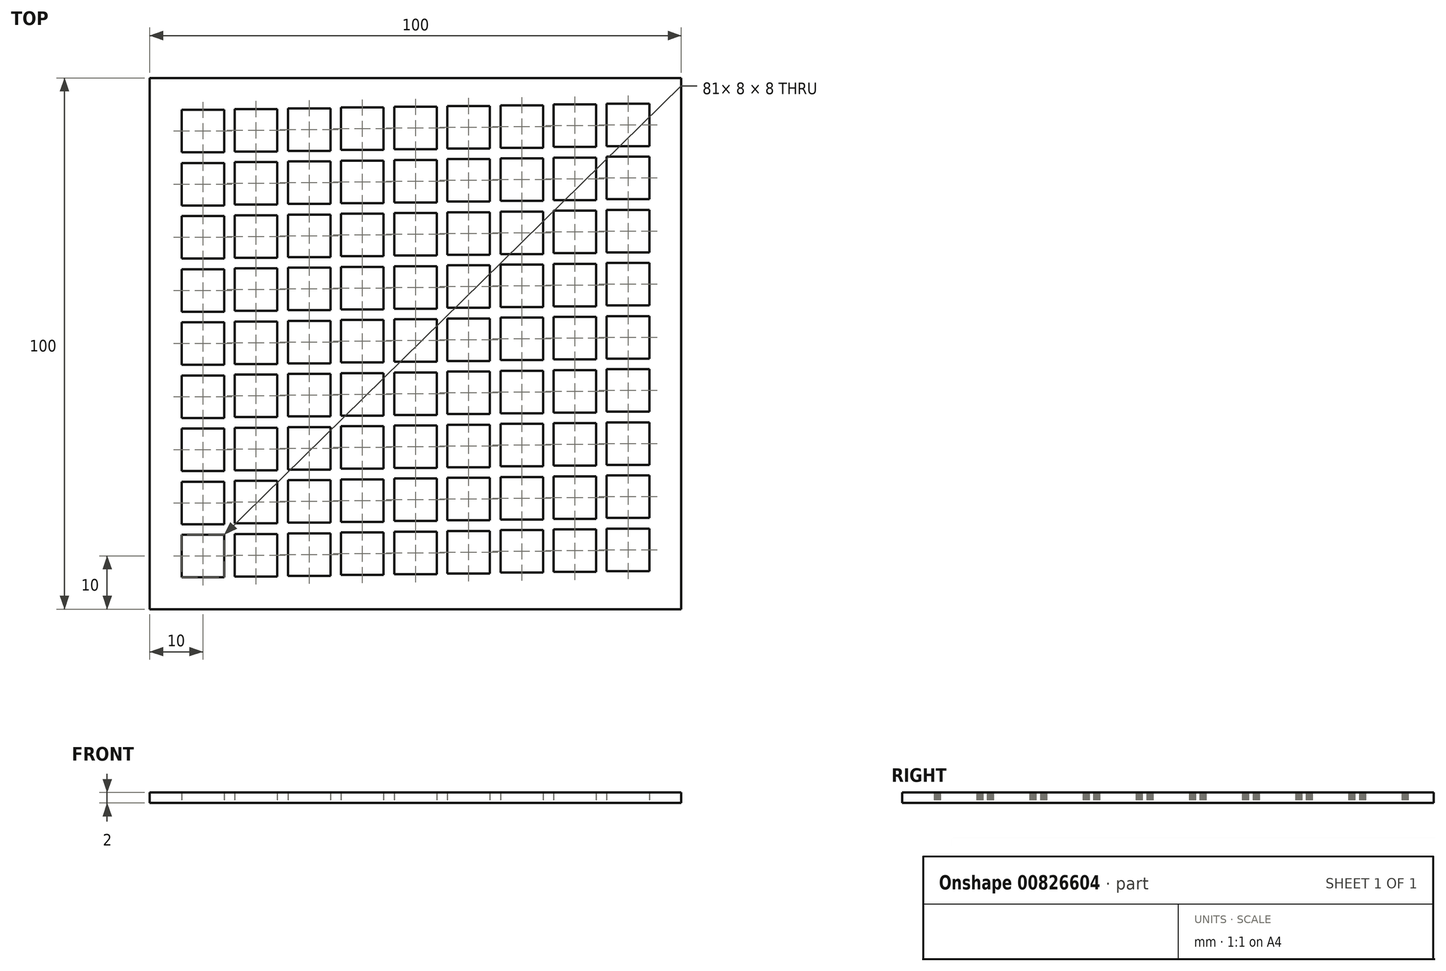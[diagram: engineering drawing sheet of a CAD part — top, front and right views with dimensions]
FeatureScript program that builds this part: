
annotation { "Feature Type Name" : "Feature", "Feature Type Description" : "" }
export const myFeature = defineFeature(function(context is Context, id is Id, definition is map)
    precondition{}
    {
        {
            var Q0;
            Q0=qCreatedBy(makeId("Top.planeOp"),FACE);
            var sketch = newSketch(context, id + "F0", { "sketchPlane" : qUnion([Q0])});
            skLineSegment(sketch, "E0.bottom", {"start": v(-50, 50) * mm, "end": v(50, 50) * mm});
            skLineSegment(sketch, "E0.top", {"start": v(-50, -50) * mm, "end": v(50, -50) * mm});
            skLineSegment(sketch, "E0.left", {"start": v(-50, 50) * mm, "end": v(-50, -50) * mm});
            skLineSegment(sketch, "E0.right", {"start": v(50, 50) * mm, "end": v(50, -50) * mm});
            skLineSegment(sketch, "E1", {"start": v(-50, 50) * mm, "end": v(50, -50) * mm, "construction": true});
            skLineSegment(sketch, "E2", {"start": v(50, 50) * mm, "end": v(-50, -50) * mm, "construction": true});
            skPoint(sketch, "E3", {"position": v(0, 0) * mm});
            skSolve(sketch);
        }
        {
            var Q0;
            Q0 = qSketchRegion(id + "F0", true);
            extrude(context, id + "F1", {"entities" : qUnion([Q0]), "depth" : 2 * mm, "offsetDistance" : 25 * mm});
        }
        {
            var Q0;
            Q0=qCreatedBy(makeId("Top.planeOp"),FACE);
            var sketch = newSketch(context, id + "F2", { "sketchPlane" : qUnion([Q0])});
            skLineSegment(sketch, "E4.bottom", {"start": v(-44, 44) * mm, "end": v(-36, 44) * mm});
            skLineSegment(sketch, "E4.top", {"start": v(-44, 36) * mm, "end": v(-36, 36) * mm});
            skLineSegment(sketch, "E4.left", {"start": v(-44, 44) * mm, "end": v(-44, 36) * mm});
            skLineSegment(sketch, "E4.right", {"start": v(-36, 44) * mm, "end": v(-36, 36) * mm});
            skLineSegment(sketch, "E5.0.1.0", {"start": v(-44, 34) * mm, "end": v(-36, 34) * mm});
            skLineSegment(sketch, "E5.0.1.1", {"start": v(-44, 26) * mm, "end": v(-36, 26) * mm});
            skLineSegment(sketch, "E5.0.1.2", {"start": v(-44, 34) * mm, "end": v(-44, 26) * mm});
            skLineSegment(sketch, "E5.0.1.3", {"start": v(-36, 34) * mm, "end": v(-36, 26) * mm});
            skLineSegment(sketch, "E5.0.2.0", {"start": v(-44, 24) * mm, "end": v(-36, 24) * mm});
            skLineSegment(sketch, "E5.0.2.1", {"start": v(-44, 16) * mm, "end": v(-36, 16) * mm});
            skLineSegment(sketch, "E5.0.2.2", {"start": v(-44, 24) * mm, "end": v(-44, 16) * mm});
            skLineSegment(sketch, "E5.0.2.3", {"start": v(-36, 24) * mm, "end": v(-36, 16) * mm});
            skLineSegment(sketch, "E5.0.3.0", {"start": v(-44, 14) * mm, "end": v(-36, 14) * mm});
            skLineSegment(sketch, "E5.0.3.1", {"start": v(-44, 6) * mm, "end": v(-36, 6) * mm});
            skLineSegment(sketch, "E5.0.3.2", {"start": v(-44, 14) * mm, "end": v(-44, 6) * mm});
            skLineSegment(sketch, "E5.0.3.3", {"start": v(-36, 14) * mm, "end": v(-36, 6) * mm});
            skLineSegment(sketch, "E5.0.4.0", {"start": v(-44, 4) * mm, "end": v(-36, 4) * mm});
            skLineSegment(sketch, "E5.0.4.1", {"start": v(-44, -4) * mm, "end": v(-36, -4) * mm});
            skLineSegment(sketch, "E5.0.4.2", {"start": v(-44, 4) * mm, "end": v(-44, -4) * mm});
            skLineSegment(sketch, "E5.0.4.3", {"start": v(-36, 4) * mm, "end": v(-36, -4) * mm});
            skLineSegment(sketch, "E5.0.5.0", {"start": v(-44, -6) * mm, "end": v(-36, -6) * mm});
            skLineSegment(sketch, "E5.0.5.1", {"start": v(-44, -14) * mm, "end": v(-36, -14) * mm});
            skLineSegment(sketch, "E5.0.5.2", {"start": v(-44, -6) * mm, "end": v(-44, -14) * mm});
            skLineSegment(sketch, "E5.0.5.3", {"start": v(-36, -6) * mm, "end": v(-36, -14) * mm});
            skLineSegment(sketch, "E5.0.6.0", {"start": v(-44, -16) * mm, "end": v(-36, -16) * mm});
            skLineSegment(sketch, "E5.0.6.1", {"start": v(-44, -24) * mm, "end": v(-36, -24) * mm});
            skLineSegment(sketch, "E5.0.6.2", {"start": v(-44, -16) * mm, "end": v(-44, -24) * mm});
            skLineSegment(sketch, "E5.0.6.3", {"start": v(-36, -16) * mm, "end": v(-36, -24) * mm});
            skLineSegment(sketch, "E5.0.7.0", {"start": v(-44, -26) * mm, "end": v(-36, -26) * mm});
            skLineSegment(sketch, "E5.0.7.1", {"start": v(-44, -34) * mm, "end": v(-36, -34) * mm});
            skLineSegment(sketch, "E5.0.7.2", {"start": v(-44, -26) * mm, "end": v(-44, -34) * mm});
            skLineSegment(sketch, "E5.0.7.3", {"start": v(-36, -26) * mm, "end": v(-36, -34) * mm});
            skLineSegment(sketch, "E5.0.8.0", {"start": v(-44, -36) * mm, "end": v(-36, -36) * mm});
            skLineSegment(sketch, "E5.0.8.1", {"start": v(-44, -44) * mm, "end": v(-36, -44) * mm});
            skLineSegment(sketch, "E5.0.8.2", {"start": v(-44, -36) * mm, "end": v(-44, -44) * mm});
            skLineSegment(sketch, "E5.0.8.3", {"start": v(-36, -36) * mm, "end": v(-36, -44) * mm});
            skLineSegment(sketch, "E5.1.0.0", {"start": v(-34, 44.14) * mm, "end": v(-26, 44.14) * mm});
            skLineSegment(sketch, "E5.1.0.1", {"start": v(-34, 36.14) * mm, "end": v(-26, 36.14) * mm});
            skLineSegment(sketch, "E5.1.0.2", {"start": v(-34, 44.14) * mm, "end": v(-34, 36.14) * mm});
            skLineSegment(sketch, "E5.1.0.3", {"start": v(-26, 44.14) * mm, "end": v(-26, 36.14) * mm});
            skLineSegment(sketch, "E5.1.1.0", {"start": v(-34, 34.14) * mm, "end": v(-26, 34.14) * mm});
            skLineSegment(sketch, "E5.1.1.1", {"start": v(-34, 26.14) * mm, "end": v(-26, 26.14) * mm});
            skLineSegment(sketch, "E5.1.1.2", {"start": v(-34, 34.14) * mm, "end": v(-34, 26.14) * mm});
            skLineSegment(sketch, "E5.1.1.3", {"start": v(-26, 34.14) * mm, "end": v(-26, 26.14) * mm});
            skLineSegment(sketch, "E5.1.2.0", {"start": v(-34, 24.14) * mm, "end": v(-26, 24.14) * mm});
            skLineSegment(sketch, "E5.1.2.1", {"start": v(-34, 16.14) * mm, "end": v(-26, 16.14) * mm});
            skLineSegment(sketch, "E5.1.2.2", {"start": v(-34, 24.14) * mm, "end": v(-34, 16.14) * mm});
            skLineSegment(sketch, "E5.1.2.3", {"start": v(-26, 24.14) * mm, "end": v(-26, 16.14) * mm});
            skLineSegment(sketch, "E5.1.3.0", {"start": v(-34, 14.14) * mm, "end": v(-26, 14.14) * mm});
            skLineSegment(sketch, "E5.1.3.1", {"start": v(-34, 6.14) * mm, "end": v(-26, 6.14) * mm});
            skLineSegment(sketch, "E5.1.3.2", {"start": v(-34, 14.14) * mm, "end": v(-34, 6.14) * mm});
            skLineSegment(sketch, "E5.1.3.3", {"start": v(-26, 14.14) * mm, "end": v(-26, 6.14) * mm});
            skLineSegment(sketch, "E5.1.4.0", {"start": v(-34, 4.14) * mm, "end": v(-26, 4.14) * mm});
            skLineSegment(sketch, "E5.1.4.1", {"start": v(-34, -3.86) * mm, "end": v(-26, -3.86) * mm});
            skLineSegment(sketch, "E5.1.4.2", {"start": v(-34, 4.14) * mm, "end": v(-34, -3.86) * mm});
            skLineSegment(sketch, "E5.1.4.3", {"start": v(-26, 4.14) * mm, "end": v(-26, -3.86) * mm});
            skLineSegment(sketch, "E5.1.5.0", {"start": v(-34, -5.86) * mm, "end": v(-26, -5.86) * mm});
            skLineSegment(sketch, "E5.1.5.1", {"start": v(-34, -13.86) * mm, "end": v(-26, -13.86) * mm});
            skLineSegment(sketch, "E5.1.5.2", {"start": v(-34, -5.86) * mm, "end": v(-34, -13.86) * mm});
            skLineSegment(sketch, "E5.1.5.3", {"start": v(-26, -5.86) * mm, "end": v(-26, -13.86) * mm});
            skLineSegment(sketch, "E5.1.6.0", {"start": v(-34, -15.86) * mm, "end": v(-26, -15.86) * mm});
            skLineSegment(sketch, "E5.1.6.1", {"start": v(-34, -23.86) * mm, "end": v(-26, -23.86) * mm});
            skLineSegment(sketch, "E5.1.6.2", {"start": v(-34, -15.86) * mm, "end": v(-34, -23.86) * mm});
            skLineSegment(sketch, "E5.1.6.3", {"start": v(-26, -15.86) * mm, "end": v(-26, -23.86) * mm});
            skLineSegment(sketch, "E5.1.7.0", {"start": v(-34, -25.86) * mm, "end": v(-26, -25.86) * mm});
            skLineSegment(sketch, "E5.1.7.1", {"start": v(-34, -33.86) * mm, "end": v(-26, -33.86) * mm});
            skLineSegment(sketch, "E5.1.7.2", {"start": v(-34, -25.86) * mm, "end": v(-34, -33.86) * mm});
            skLineSegment(sketch, "E5.1.7.3", {"start": v(-26, -25.86) * mm, "end": v(-26, -33.86) * mm});
            skLineSegment(sketch, "E5.1.8.0", {"start": v(-34, -35.86) * mm, "end": v(-26, -35.86) * mm});
            skLineSegment(sketch, "E5.1.8.1", {"start": v(-34, -43.86) * mm, "end": v(-26, -43.86) * mm});
            skLineSegment(sketch, "E5.1.8.2", {"start": v(-34, -35.86) * mm, "end": v(-34, -43.86) * mm});
            skLineSegment(sketch, "E5.1.8.3", {"start": v(-26, -35.86) * mm, "end": v(-26, -43.86) * mm});
            skLineSegment(sketch, "E5.2.0.0", {"start": v(-24, 44.29) * mm, "end": v(-16, 44.29) * mm});
            skLineSegment(sketch, "E5.2.0.1", {"start": v(-24, 36.29) * mm, "end": v(-16, 36.29) * mm});
            skLineSegment(sketch, "E5.2.0.2", {"start": v(-24, 44.29) * mm, "end": v(-24, 36.29) * mm});
            skLineSegment(sketch, "E5.2.0.3", {"start": v(-16, 44.29) * mm, "end": v(-16, 36.29) * mm});
            skLineSegment(sketch, "E5.2.1.0", {"start": v(-24, 34.29) * mm, "end": v(-16, 34.29) * mm});
            skLineSegment(sketch, "E5.2.1.1", {"start": v(-24, 26.29) * mm, "end": v(-16, 26.29) * mm});
            skLineSegment(sketch, "E5.2.1.2", {"start": v(-24, 34.29) * mm, "end": v(-24, 26.29) * mm});
            skLineSegment(sketch, "E5.2.1.3", {"start": v(-16, 34.29) * mm, "end": v(-16, 26.29) * mm});
            skLineSegment(sketch, "E5.2.2.0", {"start": v(-24, 24.29) * mm, "end": v(-16, 24.29) * mm});
            skLineSegment(sketch, "E5.2.2.1", {"start": v(-24, 16.29) * mm, "end": v(-16, 16.29) * mm});
            skLineSegment(sketch, "E5.2.2.2", {"start": v(-24, 24.29) * mm, "end": v(-24, 16.29) * mm});
            skLineSegment(sketch, "E5.2.2.3", {"start": v(-16, 24.29) * mm, "end": v(-16, 16.29) * mm});
            skLineSegment(sketch, "E5.2.3.0", {"start": v(-24, 14.29) * mm, "end": v(-16, 14.29) * mm});
            skLineSegment(sketch, "E5.2.3.1", {"start": v(-24, 6.29) * mm, "end": v(-16, 6.29) * mm});
            skLineSegment(sketch, "E5.2.3.2", {"start": v(-24, 14.29) * mm, "end": v(-24, 6.29) * mm});
            skLineSegment(sketch, "E5.2.3.3", {"start": v(-16, 14.29) * mm, "end": v(-16, 6.29) * mm});
            skLineSegment(sketch, "E5.2.4.0", {"start": v(-24, 4.29) * mm, "end": v(-16, 4.29) * mm});
            skLineSegment(sketch, "E5.2.4.1", {"start": v(-24, -3.71) * mm, "end": v(-16, -3.71) * mm});
            skLineSegment(sketch, "E5.2.4.2", {"start": v(-24, 4.29) * mm, "end": v(-24, -3.71) * mm});
            skLineSegment(sketch, "E5.2.4.3", {"start": v(-16, 4.29) * mm, "end": v(-16, -3.71) * mm});
            skLineSegment(sketch, "E5.2.5.0", {"start": v(-24, -5.71) * mm, "end": v(-16, -5.71) * mm});
            skLineSegment(sketch, "E5.2.5.1", {"start": v(-24, -13.71) * mm, "end": v(-16, -13.71) * mm});
            skLineSegment(sketch, "E5.2.5.2", {"start": v(-24, -5.71) * mm, "end": v(-24, -13.71) * mm});
            skLineSegment(sketch, "E5.2.5.3", {"start": v(-16, -5.71) * mm, "end": v(-16, -13.71) * mm});
            skLineSegment(sketch, "E5.2.6.0", {"start": v(-24, -15.71) * mm, "end": v(-16, -15.71) * mm});
            skLineSegment(sketch, "E5.2.6.1", {"start": v(-24, -23.71) * mm, "end": v(-16, -23.71) * mm});
            skLineSegment(sketch, "E5.2.6.2", {"start": v(-24, -15.71) * mm, "end": v(-24, -23.71) * mm});
            skLineSegment(sketch, "E5.2.6.3", {"start": v(-16, -15.71) * mm, "end": v(-16, -23.71) * mm});
            skLineSegment(sketch, "E5.2.7.0", {"start": v(-24, -25.71) * mm, "end": v(-16, -25.71) * mm});
            skLineSegment(sketch, "E5.2.7.1", {"start": v(-24, -33.71) * mm, "end": v(-16, -33.71) * mm});
            skLineSegment(sketch, "E5.2.7.2", {"start": v(-24, -25.71) * mm, "end": v(-24, -33.71) * mm});
            skLineSegment(sketch, "E5.2.7.3", {"start": v(-16, -25.71) * mm, "end": v(-16, -33.71) * mm});
            skLineSegment(sketch, "E5.2.8.0", {"start": v(-24, -35.71) * mm, "end": v(-16, -35.71) * mm});
            skLineSegment(sketch, "E5.2.8.1", {"start": v(-24, -43.71) * mm, "end": v(-16, -43.71) * mm});
            skLineSegment(sketch, "E5.2.8.2", {"start": v(-24, -35.71) * mm, "end": v(-24, -43.71) * mm});
            skLineSegment(sketch, "E5.2.8.3", {"start": v(-16, -35.71) * mm, "end": v(-16, -43.71) * mm});
            skLineSegment(sketch, "E5.3.0.0", {"start": v(-14, 44.43) * mm, "end": v(-6, 44.43) * mm});
            skLineSegment(sketch, "E5.3.0.1", {"start": v(-14, 36.43) * mm, "end": v(-6, 36.43) * mm});
            skLineSegment(sketch, "E5.3.0.2", {"start": v(-14, 44.43) * mm, "end": v(-14, 36.43) * mm});
            skLineSegment(sketch, "E5.3.0.3", {"start": v(-6, 44.43) * mm, "end": v(-6, 36.43) * mm});
            skLineSegment(sketch, "E5.3.1.0", {"start": v(-14, 34.43) * mm, "end": v(-6, 34.43) * mm});
            skLineSegment(sketch, "E5.3.1.1", {"start": v(-14, 26.43) * mm, "end": v(-6, 26.43) * mm});
            skLineSegment(sketch, "E5.3.1.2", {"start": v(-14, 34.43) * mm, "end": v(-14, 26.43) * mm});
            skLineSegment(sketch, "E5.3.1.3", {"start": v(-6, 34.43) * mm, "end": v(-6, 26.43) * mm});
            skLineSegment(sketch, "E5.3.2.0", {"start": v(-14, 24.43) * mm, "end": v(-6, 24.43) * mm});
            skLineSegment(sketch, "E5.3.2.1", {"start": v(-14, 16.43) * mm, "end": v(-6, 16.43) * mm});
            skLineSegment(sketch, "E5.3.2.2", {"start": v(-14, 24.43) * mm, "end": v(-14, 16.43) * mm});
            skLineSegment(sketch, "E5.3.2.3", {"start": v(-6, 24.43) * mm, "end": v(-6, 16.43) * mm});
            skLineSegment(sketch, "E5.3.3.0", {"start": v(-14, 14.43) * mm, "end": v(-6, 14.43) * mm});
            skLineSegment(sketch, "E5.3.3.1", {"start": v(-14, 6.43) * mm, "end": v(-6, 6.43) * mm});
            skLineSegment(sketch, "E5.3.3.2", {"start": v(-14, 14.43) * mm, "end": v(-14, 6.43) * mm});
            skLineSegment(sketch, "E5.3.3.3", {"start": v(-6, 14.43) * mm, "end": v(-6, 6.43) * mm});
            skLineSegment(sketch, "E5.3.4.0", {"start": v(-14, 4.43) * mm, "end": v(-6, 4.43) * mm});
            skLineSegment(sketch, "E5.3.4.1", {"start": v(-14, -3.57) * mm, "end": v(-6, -3.57) * mm});
            skLineSegment(sketch, "E5.3.4.2", {"start": v(-14, 4.43) * mm, "end": v(-14, -3.57) * mm});
            skLineSegment(sketch, "E5.3.4.3", {"start": v(-6, 4.43) * mm, "end": v(-6, -3.57) * mm});
            skLineSegment(sketch, "E5.3.5.0", {"start": v(-14, -5.57) * mm, "end": v(-6, -5.57) * mm});
            skLineSegment(sketch, "E5.3.5.1", {"start": v(-14, -13.57) * mm, "end": v(-6, -13.57) * mm});
            skLineSegment(sketch, "E5.3.5.2", {"start": v(-14, -5.57) * mm, "end": v(-14, -13.57) * mm});
            skLineSegment(sketch, "E5.3.5.3", {"start": v(-6, -5.57) * mm, "end": v(-6, -13.57) * mm});
            skLineSegment(sketch, "E5.3.6.0", {"start": v(-14, -15.57) * mm, "end": v(-6, -15.57) * mm});
            skLineSegment(sketch, "E5.3.6.1", {"start": v(-14, -23.57) * mm, "end": v(-6, -23.57) * mm});
            skLineSegment(sketch, "E5.3.6.2", {"start": v(-14, -15.57) * mm, "end": v(-14, -23.57) * mm});
            skLineSegment(sketch, "E5.3.6.3", {"start": v(-6, -15.57) * mm, "end": v(-6, -23.57) * mm});
            skLineSegment(sketch, "E5.3.7.0", {"start": v(-14, -25.57) * mm, "end": v(-6, -25.57) * mm});
            skLineSegment(sketch, "E5.3.7.1", {"start": v(-14, -33.57) * mm, "end": v(-6, -33.57) * mm});
            skLineSegment(sketch, "E5.3.7.2", {"start": v(-14, -25.57) * mm, "end": v(-14, -33.57) * mm});
            skLineSegment(sketch, "E5.3.7.3", {"start": v(-6, -25.57) * mm, "end": v(-6, -33.57) * mm});
            skLineSegment(sketch, "E5.3.8.0", {"start": v(-14, -35.57) * mm, "end": v(-6, -35.57) * mm});
            skLineSegment(sketch, "E5.3.8.1", {"start": v(-14, -43.57) * mm, "end": v(-6, -43.57) * mm});
            skLineSegment(sketch, "E5.3.8.2", {"start": v(-14, -35.57) * mm, "end": v(-14, -43.57) * mm});
            skLineSegment(sketch, "E5.3.8.3", {"start": v(-6, -35.57) * mm, "end": v(-6, -43.57) * mm});
            skLineSegment(sketch, "E5.4.0.0", {"start": v(-4, 44.58) * mm, "end": v(4, 44.58) * mm});
            skLineSegment(sketch, "E5.4.0.1", {"start": v(-4, 36.58) * mm, "end": v(4, 36.58) * mm});
            skLineSegment(sketch, "E5.4.0.2", {"start": v(-4, 44.58) * mm, "end": v(-4, 36.58) * mm});
            skLineSegment(sketch, "E5.4.0.3", {"start": v(4, 44.58) * mm, "end": v(4, 36.58) * mm});
            skLineSegment(sketch, "E5.4.1.0", {"start": v(-4, 34.58) * mm, "end": v(4, 34.58) * mm});
            skLineSegment(sketch, "E5.4.1.1", {"start": v(-4, 26.58) * mm, "end": v(4, 26.58) * mm});
            skLineSegment(sketch, "E5.4.1.2", {"start": v(-4, 34.58) * mm, "end": v(-4, 26.58) * mm});
            skLineSegment(sketch, "E5.4.1.3", {"start": v(4, 34.58) * mm, "end": v(4, 26.58) * mm});
            skLineSegment(sketch, "E5.4.2.0", {"start": v(-4, 24.58) * mm, "end": v(4, 24.58) * mm});
            skLineSegment(sketch, "E5.4.2.1", {"start": v(-4, 16.58) * mm, "end": v(4, 16.58) * mm});
            skLineSegment(sketch, "E5.4.2.2", {"start": v(-4, 24.58) * mm, "end": v(-4, 16.58) * mm});
            skLineSegment(sketch, "E5.4.2.3", {"start": v(4, 24.58) * mm, "end": v(4, 16.58) * mm});
            skLineSegment(sketch, "E5.4.3.0", {"start": v(-4, 14.58) * mm, "end": v(4, 14.58) * mm});
            skLineSegment(sketch, "E5.4.3.1", {"start": v(-4, 6.58) * mm, "end": v(4, 6.58) * mm});
            skLineSegment(sketch, "E5.4.3.2", {"start": v(-4, 14.58) * mm, "end": v(-4, 6.58) * mm});
            skLineSegment(sketch, "E5.4.3.3", {"start": v(4, 14.58) * mm, "end": v(4, 6.58) * mm});
            skLineSegment(sketch, "E5.4.4.0", {"start": v(-4, 4.58) * mm, "end": v(4, 4.58) * mm});
            skLineSegment(sketch, "E5.4.4.1", {"start": v(-4, -3.42) * mm, "end": v(4, -3.42) * mm});
            skLineSegment(sketch, "E5.4.4.2", {"start": v(-4, 4.58) * mm, "end": v(-4, -3.42) * mm});
            skLineSegment(sketch, "E5.4.4.3", {"start": v(4, 4.58) * mm, "end": v(4, -3.42) * mm});
            skLineSegment(sketch, "E5.4.5.0", {"start": v(-4, -5.42) * mm, "end": v(4, -5.42) * mm});
            skLineSegment(sketch, "E5.4.5.1", {"start": v(-4, -13.42) * mm, "end": v(4, -13.42) * mm});
            skLineSegment(sketch, "E5.4.5.2", {"start": v(-4, -5.42) * mm, "end": v(-4, -13.42) * mm});
            skLineSegment(sketch, "E5.4.5.3", {"start": v(4, -5.42) * mm, "end": v(4, -13.42) * mm});
            skLineSegment(sketch, "E5.4.6.0", {"start": v(-4, -15.42) * mm, "end": v(4, -15.42) * mm});
            skLineSegment(sketch, "E5.4.6.1", {"start": v(-4, -23.42) * mm, "end": v(4, -23.42) * mm});
            skLineSegment(sketch, "E5.4.6.2", {"start": v(-4, -15.42) * mm, "end": v(-4, -23.42) * mm});
            skLineSegment(sketch, "E5.4.6.3", {"start": v(4, -15.42) * mm, "end": v(4, -23.42) * mm});
            skLineSegment(sketch, "E5.4.7.0", {"start": v(-4, -25.42) * mm, "end": v(4, -25.42) * mm});
            skLineSegment(sketch, "E5.4.7.1", {"start": v(-4, -33.42) * mm, "end": v(4, -33.42) * mm});
            skLineSegment(sketch, "E5.4.7.2", {"start": v(-4, -25.42) * mm, "end": v(-4, -33.42) * mm});
            skLineSegment(sketch, "E5.4.7.3", {"start": v(4, -25.42) * mm, "end": v(4, -33.42) * mm});
            skLineSegment(sketch, "E5.4.8.0", {"start": v(-4, -35.42) * mm, "end": v(4, -35.42) * mm});
            skLineSegment(sketch, "E5.4.8.1", {"start": v(-4, -43.42) * mm, "end": v(4, -43.42) * mm});
            skLineSegment(sketch, "E5.4.8.2", {"start": v(-4, -35.42) * mm, "end": v(-4, -43.42) * mm});
            skLineSegment(sketch, "E5.4.8.3", {"start": v(4, -35.42) * mm, "end": v(4, -43.42) * mm});
            skLineSegment(sketch, "E5.5.0.0", {"start": v(6, 44.72) * mm, "end": v(14, 44.72) * mm});
            skLineSegment(sketch, "E5.5.0.1", {"start": v(6, 36.72) * mm, "end": v(14, 36.72) * mm});
            skLineSegment(sketch, "E5.5.0.2", {"start": v(6, 44.72) * mm, "end": v(6, 36.72) * mm});
            skLineSegment(sketch, "E5.5.0.3", {"start": v(14, 44.72) * mm, "end": v(14, 36.72) * mm});
            skLineSegment(sketch, "E5.5.1.0", {"start": v(6, 34.72) * mm, "end": v(14, 34.72) * mm});
            skLineSegment(sketch, "E5.5.1.1", {"start": v(6, 26.72) * mm, "end": v(14, 26.72) * mm});
            skLineSegment(sketch, "E5.5.1.2", {"start": v(6, 34.72) * mm, "end": v(6, 26.72) * mm});
            skLineSegment(sketch, "E5.5.1.3", {"start": v(14, 34.72) * mm, "end": v(14, 26.72) * mm});
            skLineSegment(sketch, "E5.5.2.0", {"start": v(6, 24.72) * mm, "end": v(14, 24.72) * mm});
            skLineSegment(sketch, "E5.5.2.1", {"start": v(6, 16.72) * mm, "end": v(14, 16.72) * mm});
            skLineSegment(sketch, "E5.5.2.2", {"start": v(6, 24.72) * mm, "end": v(6, 16.72) * mm});
            skLineSegment(sketch, "E5.5.2.3", {"start": v(14, 24.72) * mm, "end": v(14, 16.72) * mm});
            skLineSegment(sketch, "E5.5.3.0", {"start": v(6, 14.72) * mm, "end": v(14, 14.72) * mm});
            skLineSegment(sketch, "E5.5.3.1", {"start": v(6, 6.72) * mm, "end": v(14, 6.72) * mm});
            skLineSegment(sketch, "E5.5.3.2", {"start": v(6, 14.72) * mm, "end": v(6, 6.72) * mm});
            skLineSegment(sketch, "E5.5.3.3", {"start": v(14, 14.72) * mm, "end": v(14, 6.72) * mm});
            skLineSegment(sketch, "E5.5.4.0", {"start": v(6, 4.72) * mm, "end": v(14, 4.72) * mm});
            skLineSegment(sketch, "E5.5.4.1", {"start": v(6, -3.28) * mm, "end": v(14, -3.28) * mm});
            skLineSegment(sketch, "E5.5.4.2", {"start": v(6, 4.72) * mm, "end": v(6, -3.28) * mm});
            skLineSegment(sketch, "E5.5.4.3", {"start": v(14, 4.72) * mm, "end": v(14, -3.28) * mm});
            skLineSegment(sketch, "E5.5.5.0", {"start": v(6, -5.28) * mm, "end": v(14, -5.28) * mm});
            skLineSegment(sketch, "E5.5.5.1", {"start": v(6, -13.28) * mm, "end": v(14, -13.28) * mm});
            skLineSegment(sketch, "E5.5.5.2", {"start": v(6, -5.28) * mm, "end": v(6, -13.28) * mm});
            skLineSegment(sketch, "E5.5.5.3", {"start": v(14, -5.28) * mm, "end": v(14, -13.28) * mm});
            skLineSegment(sketch, "E5.5.6.0", {"start": v(6, -15.28) * mm, "end": v(14, -15.28) * mm});
            skLineSegment(sketch, "E5.5.6.1", {"start": v(6, -23.28) * mm, "end": v(14, -23.28) * mm});
            skLineSegment(sketch, "E5.5.6.2", {"start": v(6, -15.28) * mm, "end": v(6, -23.28) * mm});
            skLineSegment(sketch, "E5.5.6.3", {"start": v(14, -15.28) * mm, "end": v(14, -23.28) * mm});
            skLineSegment(sketch, "E5.5.7.0", {"start": v(6, -25.28) * mm, "end": v(14, -25.28) * mm});
            skLineSegment(sketch, "E5.5.7.1", {"start": v(6, -33.28) * mm, "end": v(14, -33.28) * mm});
            skLineSegment(sketch, "E5.5.7.2", {"start": v(6, -25.28) * mm, "end": v(6, -33.28) * mm});
            skLineSegment(sketch, "E5.5.7.3", {"start": v(14, -25.28) * mm, "end": v(14, -33.28) * mm});
            skLineSegment(sketch, "E5.5.8.0", {"start": v(6, -35.28) * mm, "end": v(14, -35.28) * mm});
            skLineSegment(sketch, "E5.5.8.1", {"start": v(6, -43.28) * mm, "end": v(14, -43.28) * mm});
            skLineSegment(sketch, "E5.5.8.2", {"start": v(6, -35.28) * mm, "end": v(6, -43.28) * mm});
            skLineSegment(sketch, "E5.5.8.3", {"start": v(14, -35.28) * mm, "end": v(14, -43.28) * mm});
            skLineSegment(sketch, "E5.6.0.0", {"start": v(16, 44.87) * mm, "end": v(24, 44.87) * mm});
            skLineSegment(sketch, "E5.6.0.1", {"start": v(16, 36.87) * mm, "end": v(24, 36.87) * mm});
            skLineSegment(sketch, "E5.6.0.2", {"start": v(16, 44.87) * mm, "end": v(16, 36.87) * mm});
            skLineSegment(sketch, "E5.6.0.3", {"start": v(24, 44.87) * mm, "end": v(24, 36.87) * mm});
            skLineSegment(sketch, "E5.6.1.0", {"start": v(16, 34.87) * mm, "end": v(24, 34.87) * mm});
            skLineSegment(sketch, "E5.6.1.1", {"start": v(16, 26.87) * mm, "end": v(24, 26.87) * mm});
            skLineSegment(sketch, "E5.6.1.2", {"start": v(16, 34.87) * mm, "end": v(16, 26.87) * mm});
            skLineSegment(sketch, "E5.6.1.3", {"start": v(24, 34.87) * mm, "end": v(24, 26.87) * mm});
            skLineSegment(sketch, "E5.6.2.0", {"start": v(16, 24.87) * mm, "end": v(24, 24.87) * mm});
            skLineSegment(sketch, "E5.6.2.1", {"start": v(16, 16.87) * mm, "end": v(24, 16.87) * mm});
            skLineSegment(sketch, "E5.6.2.2", {"start": v(16, 24.87) * mm, "end": v(16, 16.87) * mm});
            skLineSegment(sketch, "E5.6.2.3", {"start": v(24, 24.87) * mm, "end": v(24, 16.87) * mm});
            skLineSegment(sketch, "E5.6.3.0", {"start": v(16, 14.87) * mm, "end": v(24, 14.87) * mm});
            skLineSegment(sketch, "E5.6.3.1", {"start": v(16, 6.87) * mm, "end": v(24, 6.87) * mm});
            skLineSegment(sketch, "E5.6.3.2", {"start": v(16, 14.87) * mm, "end": v(16, 6.87) * mm});
            skLineSegment(sketch, "E5.6.3.3", {"start": v(24, 14.87) * mm, "end": v(24, 6.87) * mm});
            skLineSegment(sketch, "E5.6.4.0", {"start": v(16, 4.87) * mm, "end": v(24, 4.87) * mm});
            skLineSegment(sketch, "E5.6.4.1", {"start": v(16, -3.13) * mm, "end": v(24, -3.13) * mm});
            skLineSegment(sketch, "E5.6.4.2", {"start": v(16, 4.87) * mm, "end": v(16, -3.13) * mm});
            skLineSegment(sketch, "E5.6.4.3", {"start": v(24, 4.87) * mm, "end": v(24, -3.13) * mm});
            skLineSegment(sketch, "E5.6.5.0", {"start": v(16, -5.13) * mm, "end": v(24, -5.13) * mm});
            skLineSegment(sketch, "E5.6.5.1", {"start": v(16, -13.13) * mm, "end": v(24, -13.13) * mm});
            skLineSegment(sketch, "E5.6.5.2", {"start": v(16, -5.13) * mm, "end": v(16, -13.13) * mm});
            skLineSegment(sketch, "E5.6.5.3", {"start": v(24, -5.13) * mm, "end": v(24, -13.13) * mm});
            skLineSegment(sketch, "E5.6.6.0", {"start": v(16, -15.13) * mm, "end": v(24, -15.13) * mm});
            skLineSegment(sketch, "E5.6.6.1", {"start": v(16, -23.13) * mm, "end": v(24, -23.13) * mm});
            skLineSegment(sketch, "E5.6.6.2", {"start": v(16, -15.13) * mm, "end": v(16, -23.13) * mm});
            skLineSegment(sketch, "E5.6.6.3", {"start": v(24, -15.13) * mm, "end": v(24, -23.13) * mm});
            skLineSegment(sketch, "E5.6.7.0", {"start": v(16, -25.13) * mm, "end": v(24, -25.13) * mm});
            skLineSegment(sketch, "E5.6.7.1", {"start": v(16, -33.13) * mm, "end": v(24, -33.13) * mm});
            skLineSegment(sketch, "E5.6.7.2", {"start": v(16, -25.13) * mm, "end": v(16, -33.13) * mm});
            skLineSegment(sketch, "E5.6.7.3", {"start": v(24, -25.13) * mm, "end": v(24, -33.13) * mm});
            skLineSegment(sketch, "E5.6.8.0", {"start": v(16, -35.13) * mm, "end": v(24, -35.13) * mm});
            skLineSegment(sketch, "E5.6.8.1", {"start": v(16, -43.13) * mm, "end": v(24, -43.13) * mm});
            skLineSegment(sketch, "E5.6.8.2", {"start": v(16, -35.13) * mm, "end": v(16, -43.13) * mm});
            skLineSegment(sketch, "E5.6.8.3", {"start": v(24, -35.13) * mm, "end": v(24, -43.13) * mm});
            skLineSegment(sketch, "E5.7.0.0", {"start": v(26, 45.01) * mm, "end": v(34, 45.01) * mm});
            skLineSegment(sketch, "E5.7.0.1", {"start": v(26, 37.01) * mm, "end": v(34, 37.01) * mm});
            skLineSegment(sketch, "E5.7.0.2", {"start": v(26, 45.01) * mm, "end": v(26, 37.01) * mm});
            skLineSegment(sketch, "E5.7.0.3", {"start": v(34, 45.01) * mm, "end": v(34, 37.01) * mm});
            skLineSegment(sketch, "E5.7.1.0", {"start": v(26, 35.01) * mm, "end": v(34, 35.01) * mm});
            skLineSegment(sketch, "E5.7.1.1", {"start": v(26, 27.01) * mm, "end": v(34, 27.01) * mm});
            skLineSegment(sketch, "E5.7.1.2", {"start": v(26, 35.01) * mm, "end": v(26, 27.01) * mm});
            skLineSegment(sketch, "E5.7.1.3", {"start": v(34, 35.01) * mm, "end": v(34, 27.01) * mm});
            skLineSegment(sketch, "E5.7.2.0", {"start": v(26, 25.01) * mm, "end": v(34, 25.01) * mm});
            skLineSegment(sketch, "E5.7.2.1", {"start": v(26, 17.01) * mm, "end": v(34, 17.01) * mm});
            skLineSegment(sketch, "E5.7.2.2", {"start": v(26, 25.01) * mm, "end": v(26, 17.01) * mm});
            skLineSegment(sketch, "E5.7.2.3", {"start": v(34, 25.01) * mm, "end": v(34, 17.01) * mm});
            skLineSegment(sketch, "E5.7.3.0", {"start": v(26, 15.01) * mm, "end": v(34, 15.01) * mm});
            skLineSegment(sketch, "E5.7.3.1", {"start": v(26, 7.01) * mm, "end": v(34, 7.01) * mm});
            skLineSegment(sketch, "E5.7.3.2", {"start": v(26, 15.01) * mm, "end": v(26, 7.01) * mm});
            skLineSegment(sketch, "E5.7.3.3", {"start": v(34, 15.01) * mm, "end": v(34, 7.01) * mm});
            skLineSegment(sketch, "E5.7.4.0", {"start": v(26, 5.01) * mm, "end": v(34, 5.01) * mm});
            skLineSegment(sketch, "E5.7.4.1", {"start": v(26, -2.99) * mm, "end": v(34, -2.99) * mm});
            skLineSegment(sketch, "E5.7.4.2", {"start": v(26, 5.01) * mm, "end": v(26, -2.99) * mm});
            skLineSegment(sketch, "E5.7.4.3", {"start": v(34, 5.01) * mm, "end": v(34, -2.99) * mm});
            skLineSegment(sketch, "E5.7.5.0", {"start": v(26, -4.99) * mm, "end": v(34, -4.99) * mm});
            skLineSegment(sketch, "E5.7.5.1", {"start": v(26, -12.99) * mm, "end": v(34, -12.99) * mm});
            skLineSegment(sketch, "E5.7.5.2", {"start": v(26, -4.99) * mm, "end": v(26, -12.99) * mm});
            skLineSegment(sketch, "E5.7.5.3", {"start": v(34, -4.99) * mm, "end": v(34, -12.99) * mm});
            skLineSegment(sketch, "E5.7.6.0", {"start": v(26, -14.99) * mm, "end": v(34, -14.99) * mm});
            skLineSegment(sketch, "E5.7.6.1", {"start": v(26, -22.99) * mm, "end": v(34, -22.99) * mm});
            skLineSegment(sketch, "E5.7.6.2", {"start": v(26, -14.99) * mm, "end": v(26, -22.99) * mm});
            skLineSegment(sketch, "E5.7.6.3", {"start": v(34, -14.99) * mm, "end": v(34, -22.99) * mm});
            skLineSegment(sketch, "E5.7.7.0", {"start": v(26, -24.99) * mm, "end": v(34, -24.99) * mm});
            skLineSegment(sketch, "E5.7.7.1", {"start": v(26, -32.99) * mm, "end": v(34, -32.99) * mm});
            skLineSegment(sketch, "E5.7.7.2", {"start": v(26, -24.99) * mm, "end": v(26, -32.99) * mm});
            skLineSegment(sketch, "E5.7.7.3", {"start": v(34, -24.99) * mm, "end": v(34, -32.99) * mm});
            skLineSegment(sketch, "E5.7.8.0", {"start": v(26, -34.99) * mm, "end": v(34, -34.99) * mm});
            skLineSegment(sketch, "E5.7.8.1", {"start": v(26, -42.99) * mm, "end": v(34, -42.99) * mm});
            skLineSegment(sketch, "E5.7.8.2", {"start": v(26, -34.99) * mm, "end": v(26, -42.99) * mm});
            skLineSegment(sketch, "E5.7.8.3", {"start": v(34, -34.99) * mm, "end": v(34, -42.99) * mm});
            skLineSegment(sketch, "E5.8.0.0", {"start": v(36, 45.16) * mm, "end": v(44, 45.16) * mm});
            skLineSegment(sketch, "E5.8.0.1", {"start": v(36, 37.16) * mm, "end": v(44, 37.16) * mm});
            skLineSegment(sketch, "E5.8.0.2", {"start": v(36, 45.16) * mm, "end": v(36, 37.16) * mm});
            skLineSegment(sketch, "E5.8.0.3", {"start": v(44, 45.16) * mm, "end": v(44, 37.16) * mm});
            skLineSegment(sketch, "E5.8.1.0", {"start": v(36, 35.16) * mm, "end": v(44, 35.16) * mm});
            skLineSegment(sketch, "E5.8.1.1", {"start": v(36, 27.16) * mm, "end": v(44, 27.16) * mm});
            skLineSegment(sketch, "E5.8.1.2", {"start": v(36, 35.16) * mm, "end": v(36, 27.16) * mm});
            skLineSegment(sketch, "E5.8.1.3", {"start": v(44, 35.16) * mm, "end": v(44, 27.16) * mm});
            skLineSegment(sketch, "E5.8.2.0", {"start": v(36, 25.16) * mm, "end": v(44, 25.16) * mm});
            skLineSegment(sketch, "E5.8.2.1", {"start": v(36, 17.16) * mm, "end": v(44, 17.16) * mm});
            skLineSegment(sketch, "E5.8.2.2", {"start": v(36, 25.16) * mm, "end": v(36, 17.16) * mm});
            skLineSegment(sketch, "E5.8.2.3", {"start": v(44, 25.16) * mm, "end": v(44, 17.16) * mm});
            skLineSegment(sketch, "E5.8.3.0", {"start": v(36, 15.16) * mm, "end": v(44, 15.16) * mm});
            skLineSegment(sketch, "E5.8.3.1", {"start": v(36, 7.16) * mm, "end": v(44, 7.16) * mm});
            skLineSegment(sketch, "E5.8.3.2", {"start": v(36, 15.16) * mm, "end": v(36, 7.16) * mm});
            skLineSegment(sketch, "E5.8.3.3", {"start": v(44, 15.16) * mm, "end": v(44, 7.16) * mm});
            skLineSegment(sketch, "E5.8.4.0", {"start": v(36, 5.16) * mm, "end": v(44, 5.16) * mm});
            skLineSegment(sketch, "E5.8.4.1", {"start": v(36, -2.84) * mm, "end": v(44, -2.84) * mm});
            skLineSegment(sketch, "E5.8.4.2", {"start": v(36, 5.16) * mm, "end": v(36, -2.84) * mm});
            skLineSegment(sketch, "E5.8.4.3", {"start": v(44, 5.16) * mm, "end": v(44, -2.84) * mm});
            skLineSegment(sketch, "E5.8.5.0", {"start": v(36, -4.84) * mm, "end": v(44, -4.84) * mm});
            skLineSegment(sketch, "E5.8.5.1", {"start": v(36, -12.84) * mm, "end": v(44, -12.84) * mm});
            skLineSegment(sketch, "E5.8.5.2", {"start": v(36, -4.84) * mm, "end": v(36, -12.84) * mm});
            skLineSegment(sketch, "E5.8.5.3", {"start": v(44, -4.84) * mm, "end": v(44, -12.84) * mm});
            skLineSegment(sketch, "E5.8.6.0", {"start": v(36, -14.84) * mm, "end": v(44, -14.84) * mm});
            skLineSegment(sketch, "E5.8.6.1", {"start": v(36, -22.84) * mm, "end": v(44, -22.84) * mm});
            skLineSegment(sketch, "E5.8.6.2", {"start": v(36, -14.84) * mm, "end": v(36, -22.84) * mm});
            skLineSegment(sketch, "E5.8.6.3", {"start": v(44, -14.84) * mm, "end": v(44, -22.84) * mm});
            skLineSegment(sketch, "E5.8.7.0", {"start": v(36, -24.84) * mm, "end": v(44, -24.84) * mm});
            skLineSegment(sketch, "E5.8.7.1", {"start": v(36, -32.84) * mm, "end": v(44, -32.84) * mm});
            skLineSegment(sketch, "E5.8.7.2", {"start": v(36, -24.84) * mm, "end": v(36, -32.84) * mm});
            skLineSegment(sketch, "E5.8.7.3", {"start": v(44, -24.84) * mm, "end": v(44, -32.84) * mm});
            skLineSegment(sketch, "E5.8.8.0", {"start": v(36, -34.84) * mm, "end": v(44, -34.84) * mm});
            skLineSegment(sketch, "E5.8.8.1", {"start": v(36, -42.84) * mm, "end": v(44, -42.84) * mm});
            skLineSegment(sketch, "E5.8.8.2", {"start": v(36, -34.84) * mm, "end": v(36, -42.84) * mm});
            skLineSegment(sketch, "E5.8.8.3", {"start": v(44, -34.84) * mm, "end": v(44, -42.84) * mm});
            skLineSegment(sketch, "E5.direction1", {"start": v(-44, 36) * mm, "end": v(-34, 36.14) * mm, "construction": true});
            skLineSegment(sketch, "E5.direction2", {"start": v(-44, 36) * mm, "end": v(-44, 26) * mm, "construction": true});
            skSolve(sketch);
        }
        {
            var Q0;
            Q0 = qSketchRegion(id + "F2", true);
            extrude(context, id + "F3", {"entities" : qUnion([Q0]), "operationType" : NewBodyOperationType.REMOVE, "depth" : 2 * mm, "offsetDistance" : 25 * mm});
        }
    });
